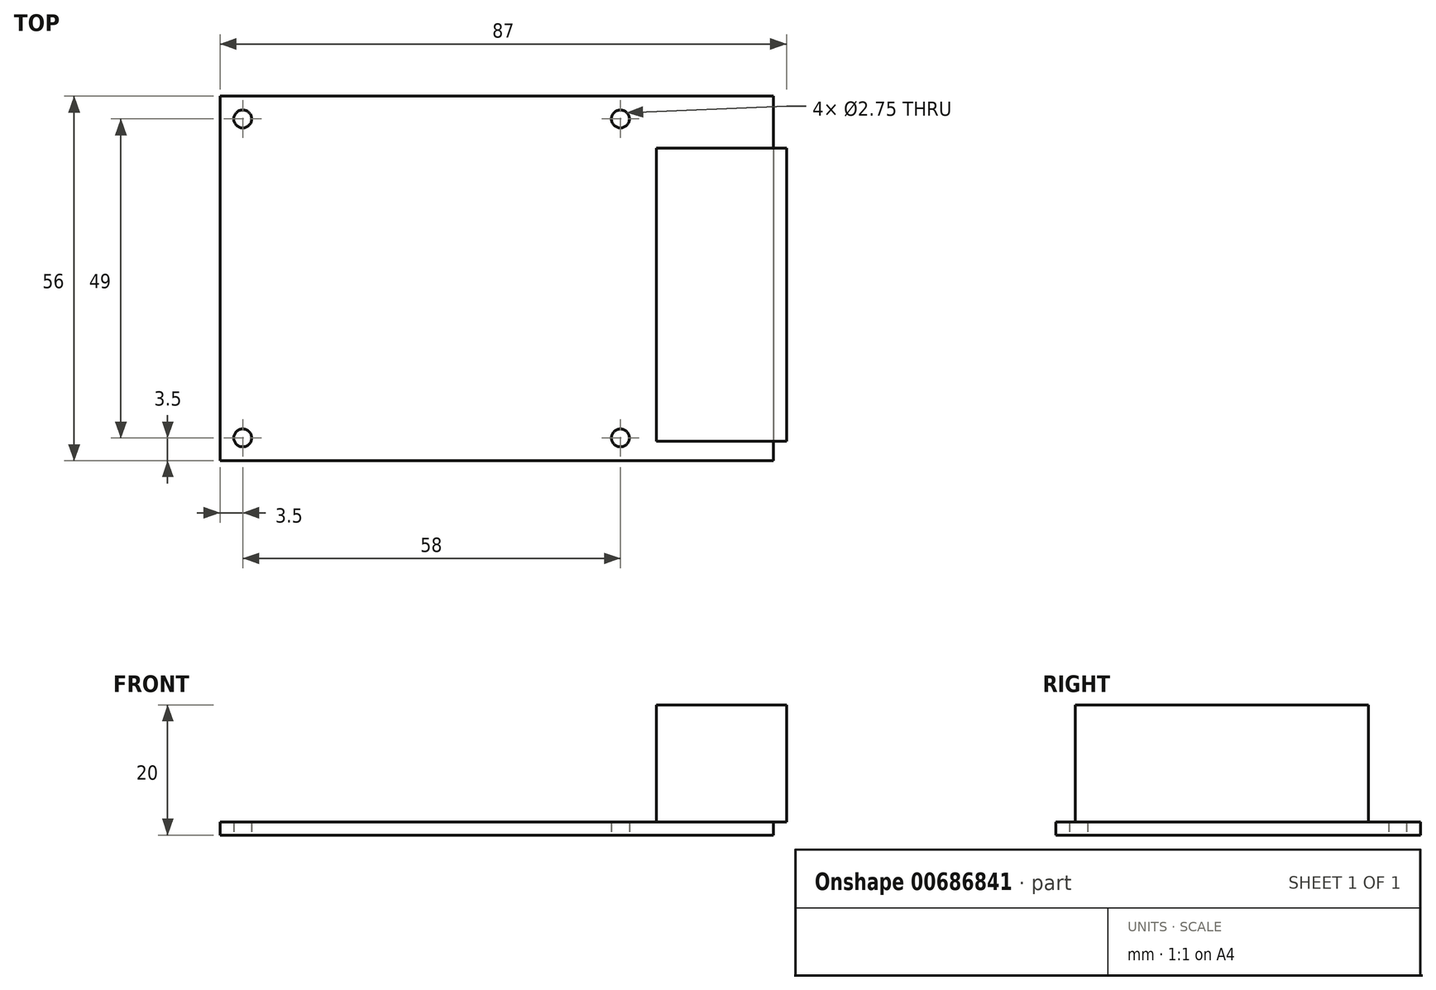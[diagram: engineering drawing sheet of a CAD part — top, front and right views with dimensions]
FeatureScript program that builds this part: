
annotation { "Feature Type Name" : "Feature", "Feature Type Description" : "" }
export const myFeature = defineFeature(function(context is Context, id is Id, definition is map)
    precondition{}
    {
        {
            var Q0;
            Q0=qCreatedBy(makeId("Top.planeOp"),FACE);
            var sketch = newSketch(context, id + "F0", { "sketchPlane" : qUnion([Q0])});
            skLineSegment(sketch, "E0.bottom", {"start": v(42.5, 28) * mm, "end": v(-42.5, 28) * mm});
            skLineSegment(sketch, "E0.top", {"start": v(42.5, -28) * mm, "end": v(-42.5, -28) * mm});
            skLineSegment(sketch, "E0.left", {"start": v(42.5, 28) * mm, "end": v(42.5, -28) * mm});
            skLineSegment(sketch, "E0.right", {"start": v(-42.5, 28) * mm, "end": v(-42.5, -28) * mm});
            skPoint(sketch, "E0.middle", {"position": v(0, 0) * mm});
            skLineSegment(sketch, "E1.bottom", {"start": v(-39, 24.5) * mm, "end": v(19, 24.5) * mm, "construction": true});
            skLineSegment(sketch, "E1.top", {"start": v(-39, -24.5) * mm, "end": v(19, -24.5) * mm, "construction": true});
            skLineSegment(sketch, "E1.left", {"start": v(-39, 24.5) * mm, "end": v(-39, -24.5) * mm, "construction": true});
            skLineSegment(sketch, "E1.right", {"start": v(19, 24.5) * mm, "end": v(19, -24.5) * mm, "construction": true});
            skCircle(sketch, "E2", {"center": v(-39, 24.5) * mm, "radius": 1.38 * mm});
            skCircle(sketch, "E3", {"center": v(19, 24.5) * mm, "radius": 1.38 * mm});
            skCircle(sketch, "E4", {"center": v(19, -24.5) * mm, "radius": 1.38 * mm});
            skCircle(sketch, "E5", {"center": v(-39, -24.5) * mm, "radius": 1.38 * mm});
            skSolve(sketch);
        }
        {
            var Q0;
            Q0=makeQuery(id+"F0.imprint","IMPRINT",FACE,{"disambiguationData":[TD([[makeQuery(id+"F0.imprint","IMPRINT",EDGE,{"derivedFrom":sQuery(id+"F0.wireOp",EDGE,"E0.bottom")}),1.0]])]});
            extrude(context, id + "F1", {"entities" : qUnion([Q0]), "depth" : 2 * mm, "offsetDistance" : 25 * mm});
        }
        {
            var Q0;
            Q0=makeQuery(id+"F1.opExtrude","CAP_FACE",FACE,{"disambiguationData":[OSD([sQuery(id+"F0.wireOp",EDGE,"E0.bottom"),sQuery(id+"F0.wireOp",EDGE,"E0.top"),sQuery(id+"F0.wireOp",EDGE,"E0.left"),sQuery(id+"F0.wireOp",EDGE,"E0.right"),sQuery(id+"F0.wireOp",EDGE,"E2"),sQuery(id+"F0.wireOp",EDGE,"E3"),sQuery(id+"F0.wireOp",EDGE,"E4"),sQuery(id+"F0.wireOp",EDGE,"E5")])],"isStart":false});
            var sketch = newSketch(context, id + "F2", { "sketchPlane" : qUnion([Q0])});
            skLineSegment(sketch, "E6.bottom", {"start": v(24.5, 20) * mm, "end": v(44.5, 20) * mm});
            skLineSegment(sketch, "E6.top", {"start": v(24.5, -25) * mm, "end": v(44.5, -25) * mm});
            skLineSegment(sketch, "E6.left", {"start": v(24.5, 20) * mm, "end": v(24.5, -25) * mm});
            skLineSegment(sketch, "E6.right", {"start": v(44.5, 20) * mm, "end": v(44.5, -25) * mm});
            skSolve(sketch);
        }
        {
            var Q0;
            Q0 = qSketchRegion(id + "F2", true);
            extrude(context, id + "F3", {"entities" : qUnion([Q0]), "depth" : 18 * mm, "offsetDistance" : 25 * mm});
        }
    });
